# Revit family: 3451A_NX_Room_Controller
name_source: partatom
category: Communication Devices
revit_build: Autodesk Revit 2014 (Build: 20130308_1515(x64)
units: mm (PartAtom-declared; Revit-internal decimal feet)

## types (1)
- 3451A_NX_Room_Controller
    Assembly Code = D5090
    Certification = Conforms with UL916 and Certified to CAN/CSA C22.2 No. 205-M1983
IC Approved
Title 24 compliance
    Controls - Intergral Sensors = NX Occupancy Sensors, Daylight Sensors and Smart Switch Stations
    Default Elevation = 48 "
    Description = The NX Room Controller is the central component of the NX room control solution.
    Dimming = Class 2 0-10VDC, 60mA per channel
For use with low voltage, two-wire dimming ballast and LED drivers
    Features = Single or dual relay versions for On/Off
• Zero-cross switching technology extends relay contact life
• Suitable for use with controlled receptacles
• Optional full range dimming control
• Override push button and status LED per relay/dimmer
• Auto configuration support for NX Occupancy Sensors, Daylight Sensors
and Smart Switch Stations
• Advanced configuration with NXBTR Bluetooth* Radio Module and smart
phone App
• Device intelligently and automatically responds to sensors and switches in
the most energy-efficient manner
• Join NX Room Controllers with CAT5 for additional loads
• Schedules are held in the devices themselves (requires optional network
connection or NXBTC Bluetooth Radio Module with real time clock)
• Retains data during power outages
• Five-year limited warranty
• 120/277/347VAC universal voltage
• Delivers simplified configuration and control of Hubbell Lighting
luminaires using SpectraSync™ color tuning technology
    Housing Material = Plastic - Hubbell - Blue
    L = 5.26 "
    Manufacturer = Hubbell Control Solutions
    Model = NX Room Controller
    Product Documentation Link = https://hubbellcdn.com
    Product Page URL = https://www.hubbell.com
    Standby Power = 120VAC: 1.2,277VAC: 1.5,347VAC: 1.5
    Type Comments = NX Room Controller
    URL = https://www.hubbell.com
    Voltage = 120/277/347 VAC
    Warranty = 5-Years Warranty
    Washer = Metal-Hubbell-Galvanized_Steel

## geometry (parser evidence)
native form markers: Sweep x1
no freeform markers — native parametric forms only
